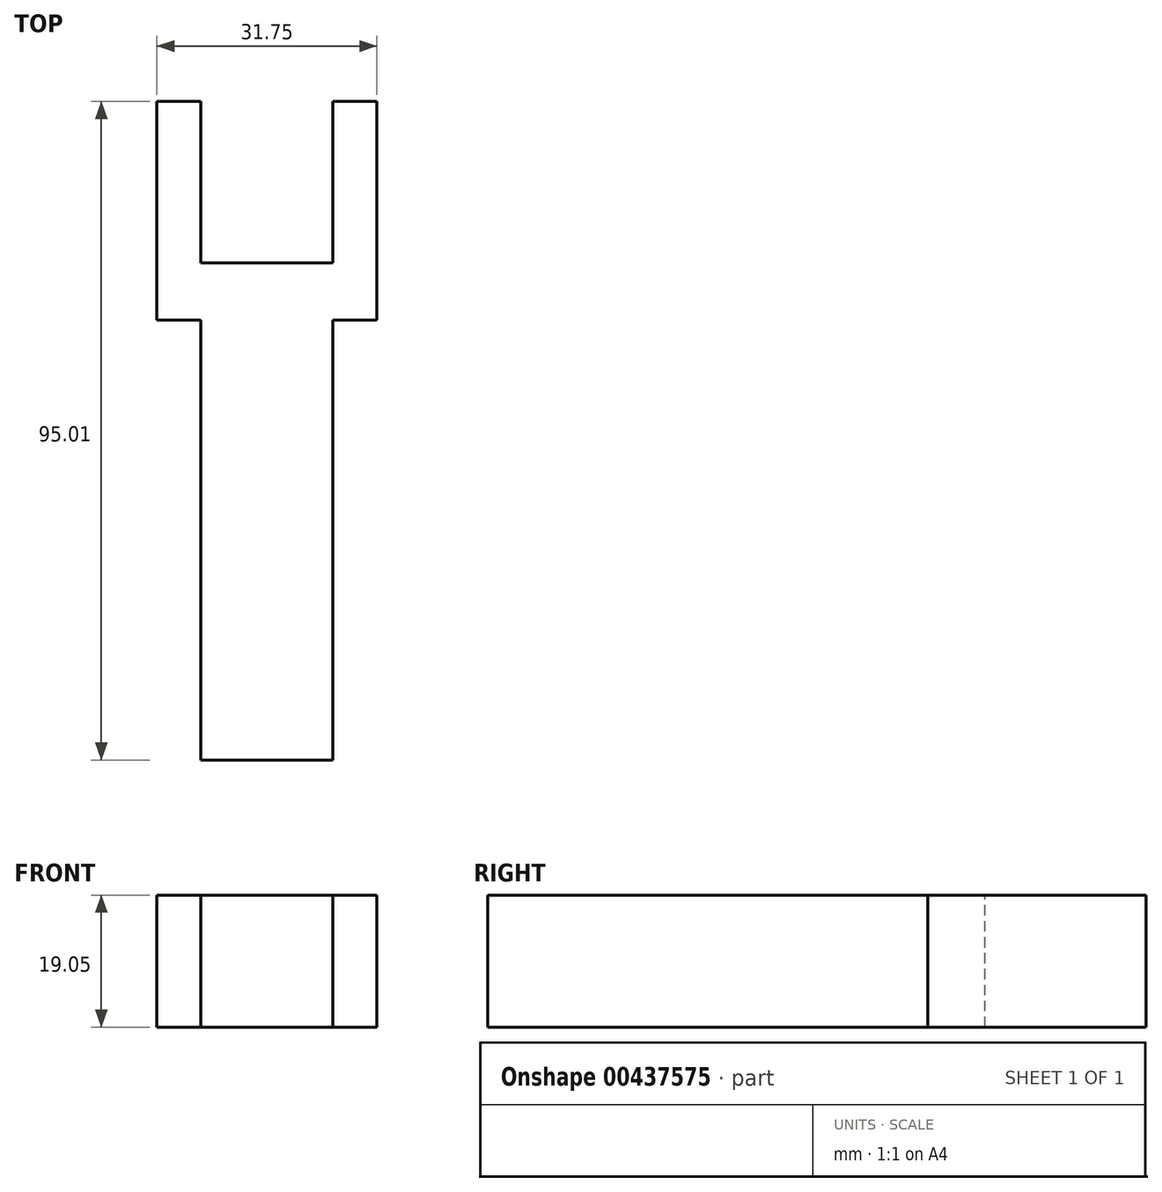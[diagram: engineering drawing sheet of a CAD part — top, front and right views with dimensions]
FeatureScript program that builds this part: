
annotation { "Feature Type Name" : "Feature", "Feature Type Description" : "" }
export const myFeature = defineFeature(function(context is Context, id is Id, definition is map)
    precondition{}
    {
        {
            var Q0;
            Q0=qCreatedBy(makeId("Front.planeOp"),FACE);
            var sketch = newSketch(context, id + "F0", { "sketchPlane" : qUnion([Q0])});
            skLineSegment(sketch, "E0.bottom", {"start": v(-30.82, 34.32) * mm, "end": v(-11.77, 34.32) * mm});
            skLineSegment(sketch, "E0.top", {"start": v(-30.82, 15.27) * mm, "end": v(-11.77, 15.27) * mm});
            skLineSegment(sketch, "E0.left", {"start": v(-30.82, 34.32) * mm, "end": v(-30.82, 15.27) * mm});
            skLineSegment(sketch, "E0.right", {"start": v(-11.77, 34.32) * mm, "end": v(-11.77, 15.27) * mm});
            skSolve(sketch);
        }
        {
            var Q0;
            Q0=makeQuery(id+"F0.imprint","IMPRINT",FACE,{"disambiguationData":[TD([[makeQuery(id+"F0.imprint","IMPRINT",EDGE,{"derivedFrom":sQuery(id+"F0.wireOp",EDGE,"E0.bottom")}),-1.0]])]});
            extrude(context, id + "F1", {"entities" : qUnion([Q0]), "depth" : 63.5 * mm});
        }
        {
            var Q0;
            Q0=makeQuery(id+"F1.opExtrude","SWEPT_FACE",FACE,{"disambiguationData":[OSD([sQuery(id+"F0.wireOp",EDGE,"E0.bottom")])]});
            var sketch = newSketch(context, id + "F2", { "sketchPlane" : qUnion([Q0])});
            skLineSegment(sketch, "E1", {"start": v(-11.77, 0) * mm, "end": v(-5.42, 0) * mm});
            skLineSegment(sketch, "E2", {"start": v(-5.42, 0) * mm, "end": v(-5.42, 31.5) * mm});
            skLineSegment(sketch, "E3", {"start": v(-37.17, 31.5) * mm, "end": v(-37.17, 0) * mm});
            skLineSegment(sketch, "E4", {"start": v(-37.17, 0) * mm, "end": v(-30.82, 0) * mm});
            skPoint(sketch, "E5.endSnap0", {"position": v(-34, 0) * mm});
            skLineSegment(sketch, "E6", {"start": v(-37.17, 31.5) * mm, "end": v(-30.82, 31.5) * mm});
            skLineSegment(sketch, "E7", {"start": v(-5.42, 31.5) * mm, "end": v(-11.77, 31.5) * mm});
            skLineSegment(sketch, "E8", {"start": v(-30.82, 31.5) * mm, "end": v(-30.82, 8.24) * mm});
            skLineSegment(sketch, "E9", {"start": v(-30.82, 8.24) * mm, "end": v(-11.77, 8.24) * mm});
            skLineSegment(sketch, "E10", {"start": v(-11.77, 8.24) * mm, "end": v(-11.77, 31.5) * mm});
            skSolve(sketch);
        }
        {
            var Q0;
            Q0=makeQuery(id+"F2.imprint","IMPRINT",FACE,{"disambiguationData":[TD([[makeQuery(id+"F2.imprint","IMPRINT",EDGE,{"derivedFrom":sQuery(id+"F2.wireOp",EDGE,"E1")}),1.0]])]});
            extrude(context, id + "F3", {"entities" : qUnion([Q0]), "operationType" : NewBodyOperationType.ADD, "oppositeDirection" : true, "depth" : 19.05 * mm});
        }
    });
